# Revit family: Cubby_Scranton_5Tier
name_source: partatom
category: Specialty Equipment
units: mm (PartAtom-declared; Revit-internal decimal feet)

## family parameters
Always vertical = Yes
Classification Number = 23.40.20.11.17
Cut with Voids When Loaded = No
Enable Cutting in Views = No
Maintain Annotation Orientation = No
Part Type = Normal
Room Calculation Point = No
Round Connector Dimension = Use Diameter
Shared = Yes
Work Plane-Based = Yes

## types (1)
- Cubby_Scranton_5Tier
    Assembly Code = C1030310
    Body Material = Plastic - HDPE - Scranton - Grey
    Construction Details = https://www.dropbox.com
    Default Elevation = 0' - 0"
    Description = Cubbies as Specified in 10 51 00
    Expected Lifespan (Years) = 0
    Green Building-LEED = http://www.arcat.com
    Installation-Fabrication = https://www.dropbox.com
    Keynote = 10 51 00
    Maintenance Schedule (Months) = 0
    Manufacturer = Scranton Products
    Manufacturer Fax = 800-551-6993
    Manufacturer Website = http://www.scrantonproducts.com
    Model = As Specified in 10 51 00
    Product Data = http://www.arcat.com
    Product Properties = http://www.arcat.com
    Revision = R1_11-2010
    Sales Information = https://www.scrantonproducts.com
    Send Message = http://www.arcat.com
    SpecWizard = http://www.arcat.com
    Specification = http://www.arcat.com
    Tiers = 5
    Type Comments = Custom sizes, color, and configurations available, please contact Scranton Products for more information
    URL = http://www.scrantonproducts.com
    Unit Depth = 1' - 0"
    Unit Height = 6' - 0"
    Unit Width = 1' - 0"
    Warranty Duration (Years) = 0

## geometry (parser evidence)
native form markers: Blend x34, Sweep x1
no freeform markers — native parametric forms only
